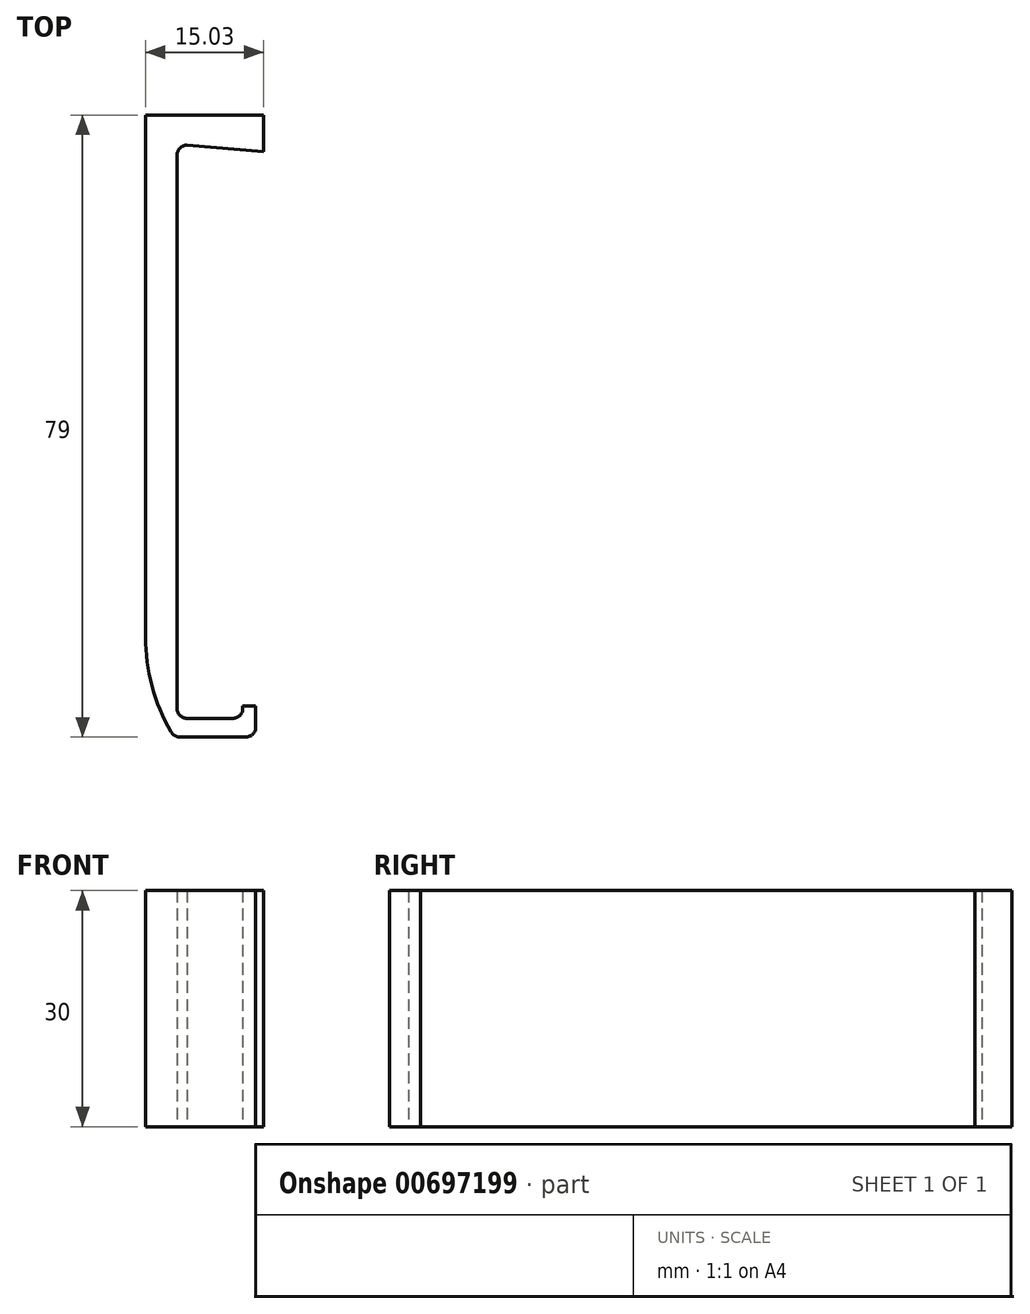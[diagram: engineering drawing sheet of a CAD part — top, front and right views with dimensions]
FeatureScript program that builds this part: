
annotation { "Feature Type Name" : "Feature", "Feature Type Description" : "" }
export const myFeature = defineFeature(function(context is Context, id is Id, definition is map)
    precondition{}
    {
        {
            var Q0;
            Q0=qCreatedBy(makeId("Top.planeOp"),FACE);
            var sketch = newSketch(context, id + "F0", { "sketchPlane" : qUnion([Q0])});
            skLineSegment(sketch, "E0", {"start": v(15, 79) * mm, "end": v(0, 79) * mm});
            skLineSegment(sketch, "E1", {"start": v(0, 79) * mm, "end": v(0, 12.7) * mm});
            skLineSegment(sketch, "E2", {"start": v(4.35, 0) * mm, "end": v(12.74, 0) * mm});
            skLineSegment(sketch, "E3", {"start": v(14.01, 1.27) * mm, "end": v(14.01, 3.91) * mm});
            skLineSegment(sketch, "E4", {"start": v(14.01, 3.91) * mm, "end": v(12.36, 3.91) * mm});
            skLineSegment(sketch, "E5", {"start": v(12.36, 3.91) * mm, "end": v(12.36, 3.63) * mm});
            skLineSegment(sketch, "E6", {"start": v(11.1, 2.36) * mm, "end": v(5.28, 2.36) * mm});
            skLineSegment(sketch, "E7", {"start": v(4.01, 3.63) * mm, "end": v(4.01, 73.92) * mm});
            skArc(sketch, "E8", {"start": v(0, 12.7) * mm, "mid": v(0.83, 6.45) * mm, "end": v(3.26, 0.63) * mm});
            skPoint(sketch, "E9.visualSharp", {"position": v(4.01, 75.2) * mm});
            skArc(sketch, "E9.filletArc", {"start": v(5.28, 75.2) * mm, "mid": v(4.39, 74.82) * mm, "end": v(4.01, 73.92) * mm});
            skPoint(sketch, "E10.visualSharp", {"position": v(4.01, 2.36) * mm});
            skArc(sketch, "E10.filletArc", {"start": v(4.01, 3.63) * mm, "mid": v(4.39, 2.73) * mm, "end": v(5.28, 2.36) * mm});
            skPoint(sketch, "E11.visualSharp", {"position": v(12.36, 2.36) * mm});
            skArc(sketch, "E11.filletArc", {"start": v(11.1, 2.36) * mm, "mid": v(12, 2.73) * mm, "end": v(12.36, 3.63) * mm});
            skPoint(sketch, "E12.visualSharp", {"position": v(14.01, 0) * mm});
            skArc(sketch, "E12.filletArc", {"start": v(12.74, 0) * mm, "mid": v(13.64, 0.37) * mm, "end": v(14.01, 1.27) * mm});
            skPoint(sketch, "E13.visualSharp", {"position": v(3.64, 0) * mm});
            skArc(sketch, "E13.filletArc", {"start": v(3.26, 0.63) * mm, "mid": v(3.72, 0.17) * mm, "end": v(4.35, 0) * mm});
            skLineSegment(sketch, "E14", {"start": v(5.28, 75.2) * mm, "end": v(15.03, 74.35) * mm});
            skLineSegment(sketch, "E15", {"start": v(15, 79) * mm, "end": v(15.03, 74.35) * mm});
            skSolve(sketch);
        }
        {
            var Q0;
            {var subQ0=sQuery(id+"F0.wireOp",EDGE,"E0");Q0=makeQuery(id+"F0.imprint","IMPRINT",FACE,{"disambiguationData":[TD([[makeQuery(id+"F0.imprint","IMPRINT",EDGE,{"derivedFrom":subQ0}),1.0]])]});}
            var Q1;
            {var subQ1=sQuery(id+"F0.wireOp",EDGE,"qHIXJff1-3Wh0-PH9r-ldJL-C7gikh6KJBhp");Q1=makeQuery(id+"F0.imprint","IMPRINT",FACE,{"disambiguationData":[TD([[makeQuery(id+"F0.imprint","IMPRINT",EDGE,{"derivedFrom":subQ1}),-1.0]])]});}
            var Q2;
            {var subQ0=sQuery(id+"F0.wireOp",EDGE,"gi8bqOLX-Dwwj-oFTu-a9fO-mPMEkuXpq5dX");Q2=makeQuery(id+"F0.imprint","IMPRINT",FACE,{"disambiguationData":[TD([[makeQuery(id+"F0.imprint","IMPRINT",EDGE,{"derivedFrom":subQ0}),-1.0]])]});}
            var Q3;
            {var subQ2=sQuery(id+"F0.wireOp",EDGE,"fJbodlRD-aKCx-ltHT-RcPX-Xq0a5cNuXHEM");Q3=makeQuery(id+"F0.imprint","IMPRINT",FACE,{"disambiguationData":[TD([[makeQuery(id+"F0.imprint","IMPRINT",EDGE,{"derivedFrom":subQ2}),-1.0]])]});}
            var Q4;
            Q4=makeQuery(id+"F0.imprint","IMPRINT",FACE,{"disambiguationData":[TD([[makeQuery(id+"F0.imprint","IMPRINT",EDGE,{"derivedFrom":sQuery(id+"F0.wireOp",EDGE,"739cebe2-dbe1-4e07-a9da-ae7837ef5df8")}),1.0]])]});
            extrude(context, id + "F1", {"entities" : qUnion([Q0, Q1, Q2, Q3, Q4]), "depth" : 30 * mm, "offsetDistance" : 25 * mm});
        }
    });
